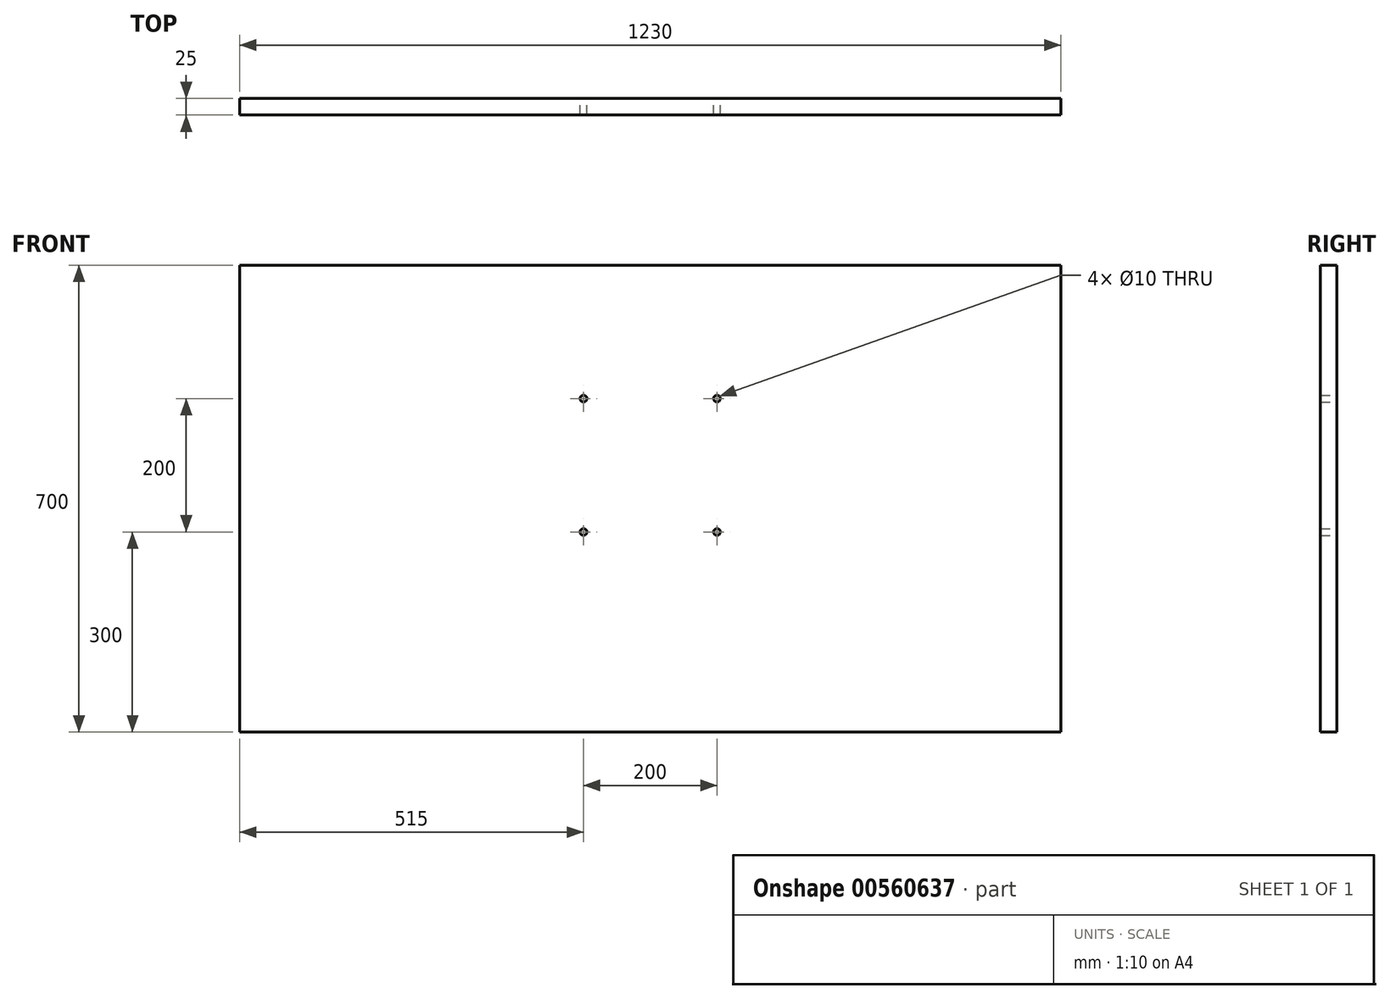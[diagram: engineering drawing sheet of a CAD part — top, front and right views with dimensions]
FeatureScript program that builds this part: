
annotation { "Feature Type Name" : "Feature", "Feature Type Description" : "" }
export const myFeature = defineFeature(function(context is Context, id is Id, definition is map)
    precondition{}
    {
        {
            var Q0;
            Q0=qCreatedBy(makeId("Front.planeOp"),FACE);
            var sketch = newSketch(context, id + "F0", { "sketchPlane" : qUnion([Q0])});
            skLineSegment(sketch, "E0.bottom", {"start": v(0, 0) * mm, "end": v(1230, 0) * mm});
            skLineSegment(sketch, "E0.top", {"start": v(0, 700) * mm, "end": v(1230, 700) * mm});
            skLineSegment(sketch, "E0.left", {"start": v(0, 0) * mm, "end": v(0, 700) * mm});
            skLineSegment(sketch, "E0.right", {"start": v(1230, 0) * mm, "end": v(1230, 700) * mm});
            skLineSegment(sketch, "E1.bottom", {"start": v(515, 500) * mm, "end": v(715, 500) * mm});
            skLineSegment(sketch, "E1.top", {"start": v(515, 300) * mm, "end": v(715, 300) * mm});
            skLineSegment(sketch, "E1.left", {"start": v(515, 500) * mm, "end": v(515, 300) * mm});
            skLineSegment(sketch, "E1.right", {"start": v(715, 500) * mm, "end": v(715, 300) * mm});
            skCircle(sketch, "E2", {"center": v(515, 500) * mm, "radius": 5 * mm});
            skCircle(sketch, "E3", {"center": v(715, 500) * mm, "radius": 5 * mm});
            skCircle(sketch, "E4", {"center": v(715, 300) * mm, "radius": 5 * mm});
            skCircle(sketch, "E5", {"center": v(515, 300) * mm, "radius": 5 * mm});
            skSolve(sketch);
        }
        {
            var Q0;
            Q0 = qSketchRegion(id + "F0", true);
            var Q1;
            {var subQ5=sQuery(id+"F0.wireOp",EDGE,"E2");var subQ13=sQuery(id+"F0.wireOp",EDGE,"E1.bottom");var subQ14=makeQuery(id+"F0.imprint","INTERSECT",VERTEX,{"derivedFrom":[subQ13,subQ5]});Q1=makeQuery(id+"F0.imprint","IMPRINT",FACE,{"disambiguationData":[TD([[makeQuery(id+"F0.imprint","IMPRINT",EDGE,{"disambiguationData":[TD([[subQ14,-1.0]])],"derivedFrom":subQ13}),-1.0]])]});}
            extrude(context, id + "F1", {"entities" : qUnion([Q0, Q1]), "depth" : 25 * mm, "offsetDistance" : 25 * mm});
        }
    });
